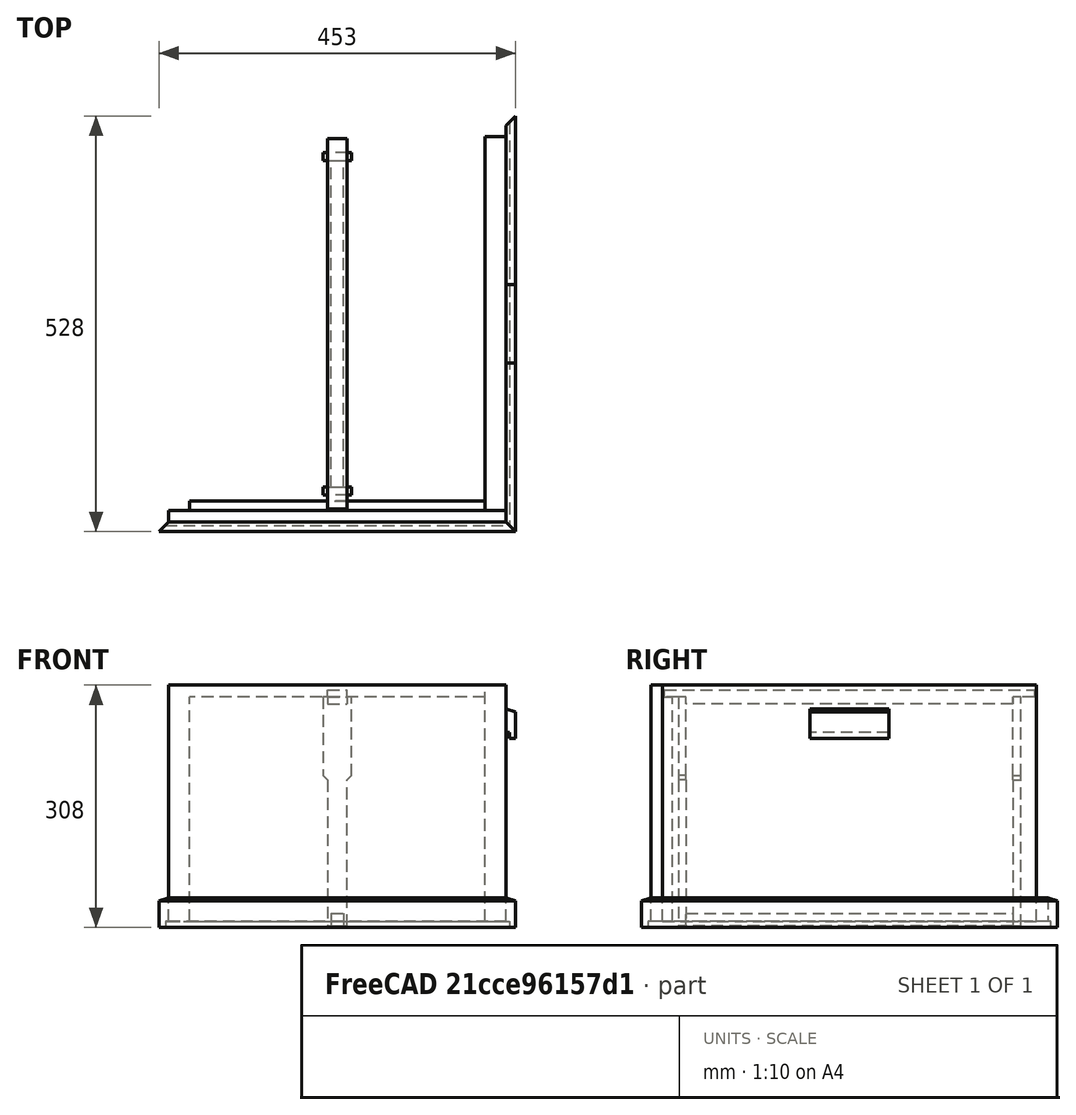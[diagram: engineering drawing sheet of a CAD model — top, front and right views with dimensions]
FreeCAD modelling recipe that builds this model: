
FCSTD DOCUMENT  (FreeCAD 0.19R)
Label: naklada
License: All rights reserved
LicenseURL: http://en.wikipedia.org/wiki/All_rights_reserved
objects: TechDraw::DrawViewDimension×33, App::Link×20, PartDesign::CoordinateSystem×16, Sketcher::SketchObject×12, TechDraw::DrawProjGroupItem×10, PartDesign::Pad×9, App::Part×7, PartDesign::Body×6, TechDraw::DrawProjGroup×5, TechDraw::DrawRichAnno×4, TechDraw::DrawViewPart×4, App::DocumentObjectGroup×3, PartDesign::Pocket×3, TechDraw::DrawSVGTemplate×3, TechDraw::DrawPage×3, TechDraw::DrawViewAnnotation×2, TechDraw::DrawViewSection×2, App::FeaturePython×1
note: 58 computed .brp shape members not serialized (recipe doc carries the construction recipe); baked Part::Feature solids carry a one-line shape summary decoded from their .brp

FEATURE [PartDesign::CoordinateSystem] LCS_Origin
  AttacherType = Attacher::AttachEngine3D
  MapMode = 2
  Support = -> [X_Axis]
FEATURE [App::FeaturePython] Variables  # WARN: FeaturePython — macro-defined, semantics opaque (R4)
  Type = App::PropertyContainer
  frame_cut = 15
  frame_height = 300
  frame_spacing = 37.5
  height = 300
  inner_depth = 450
  inner_width = 375
  wall_cut = 12.5
  wall_thickness = 27
FEATURE [App::DocumentObjectGroup] Constraints
FEATURE [App::DocumentObjectGroup] Configurations
FEATURE [PartDesign::CoordinateSystem] LCS_0
  AttacherType = Attacher::AttachEngine3D
  MapMode = 2
  Support = -> [X_Axis001]
FEATURE [PartDesign::CoordinateSystem] LCS_0001
  AttacherType = Attacher::AttachEngine3D
  MapMode = 2
  Support = -> [X_Axis002]
FEATURE [Sketcher::SketchObject] Sketch  label="Sketch001"
  FullyConstrained = true
  MapMode = 5
  Support = -> [XY_Plane002]
  expr: Constraints[16] = Variables.inner_width
  expr: Constraints[17] = Variables.wall_thickness
  expr: Constraints[22] = Variables.inner_depth / 2
  expr: Constraints[19] = Variables.wall_thickness
  expr: Constraints[18] = Variables.wall_cut
  sketch-geometry (8):
    g0: LineSegment StartX=-187.5 StartY=-225 StartZ=0 EndX=187.5 EndY=-225 EndZ=0
    g1: LineSegment StartX=187.5 StartY=-225 StartZ=0 EndX=187.5 EndY=-237.5 EndZ=0
    g2: LineSegment StartX=187.5 StartY=-237.5 StartZ=0 EndX=214.5 EndY=-237.5 EndZ=0
    g3: LineSegment StartX=214.5 StartY=-237.5 StartZ=0 EndX=214.5 EndY=-252 EndZ=0
    g4: LineSegment StartX=214.5 StartY=-252 StartZ=0 EndX=-214.5 EndY=-252 EndZ=0
    g5: LineSegment StartX=-214.5 StartY=-252 StartZ=0 EndX=-214.5 EndY=-237.5 EndZ=0
    g6: LineSegment StartX=-214.5 StartY=-237.5 StartZ=0 EndX=-187.5 EndY=-237.5 EndZ=0
    g7: LineSegment StartX=-187.5 StartY=-237.5 StartZ=0 EndX=-187.5 EndY=-225 EndZ=0
  constraints (23):
    c: Coincident(g0,g1)
    c: Coincident(g1,g2)
    c: Horizontal(g2)
    c: Coincident(g2,g3)
    c: Vertical(g3)
    c: Coincident(g3,g4)
    c: Horizontal(g4)
    c: Coincident(g4,g5)
    c: Vertical(g5)
    c: Coincident(g5,g6)
    c: Horizontal(g6)
    c: Coincident(g6,g7)
    c: Vertical(g7)
    c: Vertical(g1)
    c: Horizontal(g6,g1)
    c: Equal(g6,g2)
    c: DistanceX(g0,g0) = 375
    c: DistanceX(g2,g2) = 27
    c: DistanceY(g1,g1) = 12.5
    c: DistanceY(g3,g0) = 27
    c: Coincident(g0,g7)
    c: Symmetric(g0,g0,g-2)
    c: DistanceY(g0,g-1) = 225
FEATURE [PartDesign::Pad] Pad
  Direction = (1,1,1)
  Length = 300
  Length2 = 100
  Profile = -> Sketch
  Type = 0
  expr: Length = Variables.height
FEATURE [Sketcher::SketchObject] Sketch001  label="Sketch002"
  ExternalGeometry = -> [Pad]
  FullyConstrained = true
  MapMode = 5
  Placement = pos=(0,0,0) rot=(0.57735,0.57735,0.57735;2.0944rad)
  Support = -> [YZ_Plane002]
  expr: Constraints[9] = Variables.frame_cut
  sketch-geometry (4):
    g0: LineSegment StartX=-225 StartY=300 StartZ=0 EndX=-237.5 EndY=300 EndZ=0
    g1: LineSegment StartX=-237.5 StartY=300 StartZ=0 EndX=-237.5 EndY=285 EndZ=0
    g2: LineSegment StartX=-237.5 StartY=285 StartZ=0 EndX=-225 EndY=285 EndZ=0
    g3: LineSegment StartX=-225 StartY=285 StartZ=0 EndX=-225 EndY=300 EndZ=0
  constraints (10):
    c: Coincident(g0,g1)
    c: Coincident(g1,g2)
    c: Coincident(g2,g3)
    c: Coincident(g3,g0)
    c: Horizontal(g2)
    c: Vertical(g1)
    c: Vertical(g3)
    c: Coincident(g0,g-3)
    c: Coincident(g0,g-3)
    c: DistanceY(g3,g3) = 15
FEATURE [PartDesign::Pocket] Pocket
  BaseFeature = -> Pad
  Length = 5
  Length2 = 100
  Midplane = true
  Profile = -> Sketch001
  Type = 1
FEATURE [PartDesign::Body] Body
  Group = -> [LCS_0001,Sketch,Pad,Sketch001,Pocket]
  Origin = -> Origin002
  Tip = -> Pocket
FEATURE [App::Part] Wall_rear  label="wall_front_rear"
  Group = -> [LCS_0,Body]
  LabelDocUser = naklada
  LabelPartUser = Wall_rear
  Origin = -> Origin001
  PadLengthUser = 305.0 
  ShapeLengthUser = 890
  ShapeVolumeUser = 305.0 mm x 25.0 mm x 420.0 mm
FEATURE [App::Link] Wall_rear001  label="wall_front"
  AssemblyType = Part::Link
  AttachedBy = #LCS_0
  AttachedTo = Parent Assembly#LCS_Origin
  LinkedObject = -> Wall_rear
  SolverId = Asm4EE
  expr: Placement = LCS_Origin.Placement * AttachmentOffset * LCS_0.Placement ^ -1
FEATURE [App::Link] Wall_rear002  label="wall_rear"
  AssemblyType = Part::Link
  AttachedBy = #LCS_0
  AttachedTo = Parent Assembly#LCS_Origin
  AttachmentOffset = pos=(0,0,0) rot=(0,0,1;3.14159rad)
  LinkPlacement = pos=(0,0,0) rot=(0,0,1;3.14159rad)
  LinkedObject = -> Wall_rear
  Placement = pos=(0,0,0) rot=(0,0,1;3.14159rad)
  SolverId = Asm4EE
  expr: Placement = LCS_Origin.Placement * AttachmentOffset * LCS_0.Placement ^ -1
FEATURE [PartDesign::CoordinateSystem] LCS_0002  label="LCS_21"
  AttacherType = Attacher::AttachEngine3D
  MapMode = 2
  Support = -> [X_Axis003]
FEATURE [PartDesign::CoordinateSystem] LCS_0003
  AttacherType = Attacher::AttachEngine3D
  MapMode = 2
  Support = -> [X_Axis004]
FEATURE [Sketcher::SketchObject] Sketch002  label="Sketch003"
  FullyConstrained = true
  MapMode = 5
  Support = -> [XY_Plane004]
  expr: Constraints[6] = Variables.wall_thickness
  expr: Constraints[7] = Variables.inner_depth + Variables.wall_cut * 2
  expr: Constraints[8] = Variables.inner_width / 2
  sketch-geometry (4):
    g0: LineSegment StartX=187.5 StartY=-237.5 StartZ=0 EndX=214.5 EndY=-237.5 EndZ=0
    g1: LineSegment StartX=214.5 StartY=-237.5 StartZ=0 EndX=214.5 EndY=237.5 EndZ=0
    g2: LineSegment StartX=214.5 StartY=237.5 StartZ=0 EndX=187.5 EndY=237.5 EndZ=0
    g3: LineSegment StartX=187.5 StartY=237.5 StartZ=0 EndX=187.5 EndY=-237.5 EndZ=0
  constraints (11):
    c: Coincident(g0,g1)
    c: Coincident(g1,g2)
    c: Coincident(g2,g3)
    c: Coincident(g3,g0)
    c: Horizontal(g0)
    c: Horizontal(g2)
    c: DistanceX(g0,g0) = 27
    c: DistanceY(g1,g1) = 475
    c: DistanceX(g-1,g0) = 187.5
    c: Vertical(g1)
    c: Symmetric(g0,g2,g-1)
FEATURE [PartDesign::Pad] Pad001
  Direction = (1,1,1)
  Length = 300
  Length2 = 100
  Profile = -> Sketch002
  Type = 0
  expr: Length = Variables.height
FEATURE [PartDesign::Body] Body_2
  Group = -> [LCS_0003,Sketch002,Pad001]
  Origin = -> Origin004
  Tip = -> Pad001
FEATURE [App::Part] wall_side
  Group = -> [LCS_0002,Body_2]
  LabelDocUser = naklada
  LabelPartUser = wall_side
  Origin = -> Origin003
  PadLengthUser = 305.0 
  ShapeLengthUser = 1000
  ShapeVolumeUser = 305.0 mm x 475.0 mm x 25.0 mm
FEATURE [App::Link] wall_side001  label="wall_right"
  AssemblyType = Part::Link
  AttachedBy = #LCS_0002
  AttachedTo = Parent Assembly#LCS_Origin
  LinkedObject = -> wall_side
  SolverId = Asm4EE
  expr: Placement = LCS_Origin.Placement * AttachmentOffset * LCS_0002.Placement ^ -1
FEATURE [App::Link] wall  label="wall_left"
  AssemblyType = Part::Link
  AttachedBy = #LCS_0002
  AttachedTo = Parent Assembly#LCS_Origin
  AttachmentOffset = pos=(0,0,0) rot=(0,0,1;3.14159rad)
  LinkPlacement = pos=(0,0,0) rot=(0,0,1;3.14159rad)
  LinkedObject = -> wall_side
  Placement = pos=(0,0,0) rot=(0,0,1;3.14159rad)
  SolverId = Asm4EE
  expr: Placement = LCS_Origin.Placement * AttachmentOffset * LCS_0002.Placement ^ -1
FEATURE [PartDesign::CoordinateSystem] LCS_0004
  AttacherType = Attacher::AttachEngine3D
  MapMode = 2
  Support = -> [X_Axis005]
FEATURE [PartDesign::CoordinateSystem] LCS_0005
  AttacherType = Attacher::AttachEngine3D
  MapMode = 2
  Support = -> [X_Axis006]
FEATURE [Sketcher::SketchObject] Sketch003  label="Sketch004"
  FullyConstrained = true
  MapMode = 5
  Placement = pos=(0,0,0) rot=(1,0,0;1.5708rad)
  Support = -> [XZ_Plane006]
  expr: Constraints[12] = Variables.inner_width / 2 + Variables.wall_thickness
  sketch-geometry (6):
    g0: LineSegment StartX=214.5 StartY=0 StartZ=0 EndX=218.5 EndY=0 EndZ=0
    g1: LineSegment StartX=218.5 StartY=0 StartZ=0 EndX=218.5 EndY=-8 EndZ=0
    g2: LineSegment StartX=218.5 StartY=-8 StartZ=0 EndX=226.5 EndY=-8 EndZ=0
    g3: LineSegment StartX=226.5 StartY=-8 StartZ=0 EndX=226.5 EndY=25.6324 EndZ=0
    g4: LineSegment StartX=214.5 StartY=30 StartZ=0 EndX=214.5 EndY=0 EndZ=0
    g5: LineSegment StartX=214.5 StartY=30 StartZ=0 EndX=226.5 EndY=25.6324 EndZ=0
  constraints (18):
    c: Horizontal(g0)
    c: Coincident(g0,g1)
    c: Vertical(g1)
    c: Coincident(g1,g2)
    c: Horizontal(g2)
    c: Coincident(g2,g3)
    c: Vertical(g3)
    c: Coincident(g4,g0)
    c: Vertical(g4)
    c: DistanceX(g0,g0) = 4  'c'
    c: DistanceY(g1,g1) = 8  'd'
    c: Horizontal(g0,g-1)
    c: DistanceX(g-1,g0) = 214.5
    c: DistanceX(g0,g2) = 12  'a'
    c: DistanceY(g4,g4) = 30  'b'
    c: Coincident(g5,g4)
    c: Coincident(g5,g3)
    c: Angle(g5) = -0.349066  'e'
FEATURE [PartDesign::Pad] Pad002
  Direction = (1,1,1)
  Length = 700
  Length2 = 100
  Midplane = true
  Placement = pos=(0,0,0) rot=(1,0,0;1.5708rad)
  Profile = -> Sketch003
  Type = 0
FEATURE [Sketcher::SketchObject] Sketch004  label="Sketch005"
  ExternalGeometry = -> [Pad002]
  FullyConstrained = true
  MapMode = 5
  Support = -> [XY_Plane006]
  expr: Constraints[14] = Variables.inner_depth + 2 * Variables.wall_thickness
  sketch-geometry (8):
    g0: LineSegment StartX=226.5 StartY=-350 StartZ=0 EndX=226.5 EndY=-264 EndZ=0
    g1: LineSegment StartX=226.5 StartY=-264 StartZ=0 EndX=214.5 EndY=-252 EndZ=0
    g2: LineSegment StartX=214.5 StartY=-252 StartZ=0 EndX=214.5 EndY=-350 EndZ=0
    g3: LineSegment StartX=226.5 StartY=350 StartZ=0 EndX=226.5 EndY=264 EndZ=0
    g4: LineSegment StartX=226.5 StartY=264 StartZ=0 EndX=214.5 EndY=252 EndZ=0
    g5: LineSegment StartX=214.5 StartY=252 StartZ=0 EndX=214.5 EndY=350 EndZ=0
    g6: LineSegment StartX=214.5 StartY=-350 StartZ=0 EndX=226.5 EndY=-350 EndZ=0
    g7: LineSegment StartX=214.5 StartY=350 StartZ=0 EndX=226.5 EndY=350 EndZ=0
  constraints (20):
    c: Coincident(g0,g-4)
    c: Coincident(g1,g0)
    c: Coincident(g2,g1)
    c: Coincident(g2,g-4)
    c: Vertical(g2)
    c: Vertical(g0)
    c: Coincident(g-3,g3)
    c: Vertical(g3)
    c: Coincident(g3,g4)
    c: Coincident(g4,g5)
    c: Coincident(g5,g-3)
    c: Vertical(g5)
    c: Equal(g4,g1)
    c: Equal(g5,g2)
    c: DistanceY(g1,g4) = 504
    c: Coincident(g6,g2)
    c: Coincident(g6,g0)
    c: Coincident(g7,g5)
    c: Coincident(g7,g3)
    c: Perpendicular(g4,g1)
FEATURE [PartDesign::Pocket] Pocket001
  BaseFeature = -> Pad002
  Length = 41
  Length2 = 100
  Midplane = true
  Placement = pos=(0,0,0) rot=(1,0,0;1.5708rad)
  Profile = -> Sketch004
  Type = 1
FEATURE [PartDesign::Body] Body_3
  Group = -> [LCS_0005,Sketch003,Pad002,Sketch004,Pocket001]
  Origin = -> Origin006
  Tip = -> Pocket001
FEATURE [App::Part] Slat  label="slat_side"
  Group = -> [LCS_0004,Body_3]
  Origin = -> Origin005
FEATURE [PartDesign::CoordinateSystem] LCS_0006
  AttacherType = Attacher::AttachEngine3D
  MapMode = 2
  Support = -> [X_Axis007]
FEATURE [PartDesign::CoordinateSystem] LCS_0007
  AttacherType = Attacher::AttachEngine3D
  MapMode = 2
  Support = -> [X_Axis008]
FEATURE [Sketcher::SketchObject] Sketch005  label="Sketch006"
  FullyConstrained = true
  MapMode = 5
  Placement = pos=(0,0,0) rot=(0.57735,0.57735,0.57735;2.0944rad)
  Support = -> [YZ_Plane008]
  expr: Constraints[17] = Variables.inner_depth / 2 + Variables.wall_thickness
  sketch-geometry (6):
    g0: LineSegment StartX=-252 StartY=0 StartZ=0 EndX=-252 EndY=30 EndZ=0
    g1: LineSegment StartX=-264 StartY=25.6324 StartZ=0 EndX=-264 EndY=-8 EndZ=0
    g2: LineSegment StartX=-264 StartY=-8 StartZ=0 EndX=-256 EndY=-8 EndZ=0
    g3: LineSegment StartX=-256 StartY=-8 StartZ=0 EndX=-256 EndY=0 EndZ=0
    g4: LineSegment StartX=-256 StartY=0 StartZ=0 EndX=-252 EndY=0 EndZ=0
    g5: LineSegment StartX=-264 StartY=25.6324 StartZ=0 EndX=-252 EndY=30 EndZ=0
  constraints (18):
    c: Vertical(g0)
    c: Vertical(g1)
    c: Coincident(g1,g2)
    c: Horizontal(g2)
    c: Coincident(g2,g3)
    c: Vertical(g3)
    c: Coincident(g3,g4)
    c: Coincident(g4,g0)
    c: Horizontal(g4)
    c: Horizontal(g0,g-1)
    c: DistanceX(g4,g4) = 4
    c: DistanceY(g3,g3) = 8
    c: DistanceX(g1,g0) = 12
    c: DistanceY(g0,g0) = 30
    c: Coincident(g5,g1)
    c: Coincident(g5,g0)
    c: Angle(g5) = 0.349066
    c: DistanceX(g0,g-1) = 252
FEATURE [PartDesign::Pad] Pad003
  Direction = (1,1,1)
  Length = 700
  Length2 = 100
  Midplane = true
  Placement = pos=(0,0,0) rot=(0.57735,0.57735,0.57735;2.0944rad)
  Profile = -> Sketch005
  Type = 0
FEATURE [Sketcher::SketchObject] Sketch006  label="Sketch007"
  ExternalGeometry = -> [Pad003]
  FullyConstrained = true
  MapMode = 5
  Support = -> [XY_Plane008]
  expr: Constraints[19] = Variables.inner_width + 2 * Variables.wall_thickness
  sketch-geometry (8):
    g0: LineSegment StartX=-350 StartY=-264 StartZ=0 EndX=-350 EndY=-252 EndZ=0
    g1: LineSegment StartX=-350 StartY=-252 StartZ=0 EndX=-214.5 EndY=-252 EndZ=0
    g2: LineSegment StartX=-214.5 StartY=-252 StartZ=0 EndX=-226.5 EndY=-264 EndZ=0
    g3: LineSegment StartX=-226.5 StartY=-264 StartZ=0 EndX=-350 EndY=-264 EndZ=0
    g4: LineSegment StartX=350 StartY=-264 StartZ=0 EndX=350 EndY=-252 EndZ=0
    g5: LineSegment StartX=350 StartY=-252 StartZ=0 EndX=214.5 EndY=-252 EndZ=0
    g6: LineSegment StartX=214.5 StartY=-252 StartZ=0 EndX=226.5 EndY=-264 EndZ=0
    g7: LineSegment StartX=226.5 StartY=-264 StartZ=0 EndX=350 EndY=-264 EndZ=0
  constraints (20):
    c: Coincident(g-3,g0)
    c: Coincident(g0,g-3)
    c: Coincident(g0,g1)
    c: Coincident(g1,g2)
    c: Coincident(g2,g3)
    c: Coincident(g3,g0)
    c: Coincident(g-4,g4)
    c: Coincident(g4,g-4)
    c: Coincident(g4,g5)
    c: Coincident(g5,g6)
    c: Coincident(g6,g7)
    c: Coincident(g7,g4)
    c: Perpendicular(g2,g6)
    c: Equal(g2,g6)
    c: Equal(g1,g5)
    c: Horizontal(g1)
    c: Horizontal(g3)
    c: Horizontal(g7)
    c: Horizontal(g5)
    c: DistanceX(g1,g5) = 429
FEATURE [PartDesign::Pocket] Pocket002
  BaseFeature = -> Pad003
  Length = 5
  Length2 = 100
  Midplane = true
  Placement = pos=(0,0,0) rot=(0.57735,0.57735,0.57735;2.0944rad)
  Profile = -> Sketch006
  Type = 1
FEATURE [PartDesign::Body] Body_4
  Group = -> [LCS_0007,Sketch005,Pad003,Sketch006,Pocket002]
  Origin = -> Origin008
  Tip = -> Pocket002
FEATURE [App::Part] Slat2  label="slat_front_rear"
  Group = -> [LCS_0006,Body_4]
  Origin = -> Origin007
FEATURE [App::Link] Slat003  label="slat_right"
  AssemblyType = Part::Link
  AttachedBy = #LCS_0004
  AttachedTo = Parent Assembly#LCS_Origin
  LinkedObject = -> Slat
  SolverId = Asm4EE
  expr: Placement = LCS_Origin.Placement * AttachmentOffset * LCS_0004.Placement ^ -1
FEATURE [App::Link] Slat2001  label="slat_front"
  AssemblyType = Part::Link
  AttachedBy = #LCS_0006
  AttachedTo = Parent Assembly#LCS_Origin
  LinkedObject = -> Slat2
  SolverId = Asm4EE
  expr: Placement = LCS_Origin.Placement * AttachmentOffset * LCS_0006.Placement ^ -1
FEATURE [App::Link] Slat2002  label="slat_left"
  AssemblyType = Part::Link
  AttachedBy = #LCS_0004
  AttachedTo = Parent Assembly#LCS_Origin
  AttachmentOffset = pos=(0,0,0) rot=(0,0,1;3.14159rad)
  LinkPlacement = pos=(0,0,0) rot=(0,0,1;3.14159rad)
  LinkedObject = -> Slat
  Placement = pos=(0,0,0) rot=(0,0,1;3.14159rad)
  SolverId = Asm4EE
  expr: Placement = LCS_Origin.Placement * AttachmentOffset * LCS_0004.Placement ^ -1
FEATURE [App::Link] Slat2003  label="slat_rear"
  AssemblyType = Part::Link
  AttachedBy = #LCS_0006
  AttachedTo = Parent Assembly#LCS_Origin
  AttachmentOffset = pos=(0,0,0) rot=(0,0,1;3.14159rad)
  LinkPlacement = pos=(0,0,0) rot=(0,0,1;3.14159rad)
  LinkedObject = -> Slat2
  Placement = pos=(0,0,0) rot=(0,0,1;3.14159rad)
  SolverId = Asm4EE
  expr: Placement = LCS_Origin.Placement * AttachmentOffset * LCS_0006.Placement ^ -1
FEATURE [TechDraw::DrawSVGTemplate] Template
  EditableTexts = AVTOR=Brane Borštnik; AVTOR_2=Risal: Janez Paternoster; DATUM=6.5.2022; MATERIAL=Les, smreka; MERILO=1:5; NAZIV=Naklada; NAZIV_2=Dadant-Blatt panj; STRAN=Stran 1/3; VIR=https://github.com/<owner>/Dadant-Blatt
  Height = 297
  Orientation = 0
  Width = 210
FEATURE [Sketcher::SketchObject] Sketch007  label="Sketch008"
  FullyConstrained = true
  MapMode = 5
  Placement = pos=(0,0,0) rot=(1,0,0;1.5708rad)
  Support = -> [XZ_Plane009]
  expr: Constraints[11] = Variables.inner_width / 2 + Variables.wall_thickness
  expr: Constraints[17] = Variables.height - 30
  sketch-geometry (6):
    g0: LineSegment StartX=214.5 StartY=240 StartZ=0 EndX=218.5 EndY=240 EndZ=0
    g1: LineSegment StartX=218.5 StartY=240 StartZ=0 EndX=218.5 EndY=232 EndZ=0
    g2: LineSegment StartX=218.5 StartY=232 StartZ=0 EndX=226.5 EndY=232 EndZ=0
    g3: LineSegment StartX=226.5 StartY=232 StartZ=0 EndX=226.5 EndY=265.632 EndZ=0
    g4: LineSegment StartX=214.5 StartY=270 StartZ=0 EndX=214.5 EndY=240 EndZ=0
    g5: LineSegment StartX=214.5 StartY=270 StartZ=0 EndX=226.5 EndY=265.632 EndZ=0
  constraints (18):
    c: Horizontal(g0)
    c: Coincident(g0,g1)
    c: Vertical(g1)
    c: Coincident(g1,g2)
    c: Horizontal(g2)
    c: Coincident(g2,g3)
    c: Vertical(g3)
    c: Coincident(g4,g0)
    c: Vertical(g4)
    c: DistanceX(g0,g0) = 4  'c'
    c: DistanceY(g1,g1) = 8  'd'
    c: DistanceX(g-1,g0) = 214.5
    c: DistanceX(g0,g2) = 12  'a'
    c: DistanceY(g4,g4) = 30  'b'
    c: Coincident(g5,g4)
    c: Coincident(g5,g3)
    c: Angle(g5) = -0.349066  'e'
    c: DistanceY(g-1,g4) = 270
FEATURE [PartDesign::CoordinateSystem] LCS_0008
  AttacherType = Attacher::AttachEngine3D
  MapMode = 2
  Support = -> [X_Axis010]
FEATURE [PartDesign::CoordinateSystem] LCS_0009
  AttacherType = Attacher::AttachEngine3D
  MapMode = 2
  Support = -> [X_Axis009]
FEATURE [PartDesign::Pad] Pad004
  Direction = (1,1,1)
  Length = 100
  Length2 = 100
  Midplane = true
  Placement = pos=(0,0,0) rot=(1,0,0;1.5708rad)
  Profile = -> Sketch007
  Type = 0
FEATURE [PartDesign::Body] Body_005
  Group = -> [LCS_0008,Sketch007,Pad004]
  Origin = -> Origin009
  Tip = -> Pad004
FEATURE [App::Part] Slat2004  label="handle"
  Group = -> [LCS_0009,Body_005]
  Origin = -> Origin010
FEATURE [App::Link] Handle1  label="handle_right"
  AssemblyType = Part::Link
  AttachedBy = #LCS_0009
  AttachedTo = Parent Assembly#LCS_Origin
  LinkedObject = -> Slat2004
  SolverId = Asm4EE
  expr: Placement = LCS_Origin.Placement * AttachmentOffset * LCS_0009.Placement ^ -1
FEATURE [App::Link] Handle2  label="handle_left"
  AssemblyType = Part::Link
  AttachedBy = #LCS_0009
  AttachedTo = Parent Assembly#LCS_Origin
  AttachmentOffset = pos=(0,0,0) rot=(0,0,1;3.14159rad)
  LinkPlacement = pos=(0,0,0) rot=(0,0,1;3.14159rad)
  LinkedObject = -> Slat2004
  Placement = pos=(0,0,0) rot=(0,0,1;3.14159rad)
  SolverId = Asm4EE
  expr: Placement = LCS_Origin.Placement * AttachmentOffset * LCS_0009.Placement ^ -1
FEATURE [TechDraw::DrawSVGTemplate] Template001
  EditableTexts = AVTOR=Brane Borštnik; AVTOR_2=Risal: Janez Paternoster; DATUM=6.5.2022; MATERIAL=Les, smreka; MERILO=1:5; NAZIV=Naklada; NAZIV_2=Dadant-Blatt panj; STRAN=Stran 2/3; VIR=https://github.com/<owner>/Dadant-Blatt
  Height = 297
  Orientation = 0
  Width = 210
FEATURE [TechDraw::DrawProjGroupItem] ProjItem  label="Front"
  CoarseView = false
  Direction = (0,1,0)
  Focus = 100
  HardHidden = false
  IsoCount = 0
  IsoHidden = false
  IsoVisible = false
  LockPosition = true
  Perspective = false
  Rotation = 0
  RotationVector = (-1,0,0)
  Scale = 0.2
  ScaleType = 2
  SeamHidden = false
  SeamVisible = true
  SmoothHidden = false
  SmoothVisible = true
  Source = -> [Wall_rear]
  Type = 0
  X = 0
  XDirection = (-1,0,0)
  Y = 0
FEATURE [TechDraw::DrawProjGroupItem] ProjItem001  label="Left"
  CoarseView = false
  Direction = (1,1e-16,0)
  Focus = 100
  HardHidden = false
  IsoCount = 0
  IsoHidden = false
  IsoVisible = false
  LockPosition = false
  Perspective = false
  Rotation = 0
  RotationVector = (1,0,0)
  Scale = 0.2
  ScaleType = 2
  SeamHidden = false
  SeamVisible = true
  SmoothHidden = false
  SmoothVisible = true
  Source = -> [Wall_rear]
  Type = 1
  X = 75.6
  XDirection = (-1e-16,1,0)
  Y = 0
FEATURE [TechDraw::DrawProjGroup] ProjGroup
  Anchor = -> ProjItem
  AutoDistribute = true
  LockPosition = false
  ProjectionType = 0
  Rotation = 0
  Scale = 0.2
  ScaleType = 0
  Source = -> [Wall_rear]
  Views = -> [ProjItem,ProjItem001]
  X = 94.3849
  Y = 230.952
  spacingX = 30
  spacingY = 15
FEATURE [TechDraw::DrawViewDimension] Dimension009
  Arbitrary = false
  ArbitraryTolerances = false
  EqualTolerance = true
  FormatSpec = %.6g
  FormatSpecOverTolerance = %+.6g
  FormatSpecUnderTolerance = %+.6g
  Inverted = false
  LockPosition = false
  MeasureType = 1
  OverTolerance = 0
  References2D = -> [ProjItem]
  Rotation = 0
  ScaleType = 0
  TheoreticalExact = false
  Type = 1
  UnderTolerance = 0
  X = -0.502911
  Y = 52.7957
FEATURE [TechDraw::DrawViewDimension] Dimension010
  Arbitrary = false
  ArbitraryTolerances = false
  EqualTolerance = true
  FormatSpec = %.6g
  FormatSpecOverTolerance = %+.6g
  FormatSpecUnderTolerance = %+.6g
  Inverted = false
  LockPosition = false
  MeasureType = 1
  OverTolerance = 0
  References2D = -> [ProjItem]
  Rotation = 0
  ScaleType = 0
  TheoreticalExact = false
  Type = 1
  UnderTolerance = 0
  X = -0.502911
  Y = 44.9343
FEATURE [TechDraw::DrawViewDimension] Dimension011
  Arbitrary = false
  ArbitraryTolerances = false
  EqualTolerance = true
  FormatSpec = H = %.6g ali 200 ali 175
  FormatSpecOverTolerance = %+.6g
  FormatSpecUnderTolerance = %+.6g
  Inverted = false
  LockPosition = false
  MeasureType = 1
  OverTolerance = 0
  References2D = -> [ProjItem]
  Rotation = 0
  ScaleType = 0
  TheoreticalExact = false
  Type = 2
  UnderTolerance = 0
  X = -64.9634
  Y = 0
FEATURE [TechDraw::DrawViewDimension] Dimension013
  Arbitrary = false
  ArbitraryTolerances = false
  EqualTolerance = true
  FormatSpec = (%.6g)
  FormatSpecOverTolerance = %+.6g
  FormatSpecUnderTolerance = %+.6g
  Inverted = false
  LockPosition = false
  MeasureType = 1
  OverTolerance = 0
  References2D = -> [ProjItem]
  Rotation = 0
  ScaleType = 0
  TheoreticalExact = false
  Type = 1
  UnderTolerance = 0
  X = 51.7346
  Y = 44.9168
FEATURE [TechDraw::DrawViewDimension] Dimension014
  Arbitrary = false
  ArbitraryTolerances = false
  EqualTolerance = true
  FormatSpec = %.6g
  FormatSpecOverTolerance = %+.6g
  FormatSpecUnderTolerance = %+.6g
  Inverted = false
  LockPosition = false
  MeasureType = 1
  OverTolerance = 0
  References2D = -> [ProjItem001]
  Rotation = 0
  ScaleType = 0
  TheoreticalExact = false
  Type = 1
  UnderTolerance = 0
  X = 10.47
  Y = 52.6456
FEATURE [TechDraw::DrawViewDimension] Dimension015
  Arbitrary = false
  ArbitraryTolerances = false
  EqualTolerance = true
  FormatSpec = %.6g
  FormatSpecOverTolerance = %+.6g
  FormatSpecUnderTolerance = %+.6g
  Inverted = false
  LockPosition = false
  MeasureType = 1
  OverTolerance = 0
  References2D = -> [ProjItem001]
  Rotation = 0
  ScaleType = 0
  TheoreticalExact = false
  Type = 1
  UnderTolerance = 0
  X = 11.2317
  Y = 44.9255
FEATURE [TechDraw::DrawRichAnno] RichTextAnnotation
  AnnoParent = -> ProjItem
  AnnoText = <!DOCTYPE HTML PUBLIC "-//W3C//DTD HTML 4.0//EN" "http://www.w3.org/TR/REC-html40/strict.dtd">\n<html><head><meta name="qrichtext" content="1" /><style type="text/css">\np, li { white-space: pre-wrap; }\n</style></head><body style=" font-family:'Ubuntu'; font-size:11pt; font-weight:400; font-style:normal;">\n<p style=" margin-top:0px; margin-bottom:0px; margin-left:0px; margin-right:0px; -qt-block-indent:0; text-indent:0px;"><span style=" font-size:10pt;">Sprednja in</span></p>\n<p style=" margin-top:0px; margin-bottom:0px; margin-left:0px; margin-right:0px; -qt-block-indent:0; text-indent:0px;"><span style=" font-size:10pt;">zadnja stranica</span></p></body></html>
  LockPosition = false
  MaxWidth = -1
  Rotation = 0
  ScaleType = 0
  ShowFrame = false
  X = 0
  Y = 0
FEATURE [TechDraw::DrawProjGroupItem] ProjItem002  label="Front001"
  CoarseView = false
  Direction = (1,0,0)
  Focus = 100
  HardHidden = false
  IsoCount = 0
  IsoHidden = false
  IsoVisible = false
  LockPosition = true
  Perspective = false
  Rotation = 0
  RotationVector = (0,1,0)
  Scale = 0.2
  ScaleType = 2
  SeamHidden = false
  SeamVisible = true
  SmoothHidden = false
  SmoothVisible = true
  Source = -> [wall_side]
  Type = 0
  X = 0
  XDirection = (0,1,0)
  Y = 0
FEATURE [TechDraw::DrawProjGroupItem] ProjItem003  label="Left001"
  CoarseView = false
  Direction = (1e-16,-1,0)
  Focus = 100
  HardHidden = false
  IsoCount = 0
  IsoHidden = false
  IsoVisible = false
  LockPosition = false
  Perspective = false
  Rotation = 0
  RotationVector = (1,0,0)
  Scale = 0.2
  ScaleType = 2
  SeamHidden = false
  SeamVisible = true
  SmoothHidden = false
  SmoothVisible = true
  Source = -> [wall_side]
  Type = 1
  X = 80.2
  XDirection = (1,1e-16,0)
  Y = 0
FEATURE [TechDraw::DrawProjGroup] ProjGroup001
  Anchor = -> ProjItem002
  AutoDistribute = true
  LockPosition = false
  ProjectionType = 0
  Rotation = 0
  Scale = 0.2
  ScaleType = 0
  Source = -> [wall_side]
  Views = -> [ProjItem002,ProjItem003]
  X = 91.8443
  Y = 140.877
  spacingX = 30
  spacingY = 15
FEATURE [TechDraw::DrawViewDimension] Dimension016
  Arbitrary = false
  ArbitraryTolerances = false
  EqualTolerance = true
  FormatSpec = %.6g
  FormatSpecOverTolerance = %+.6g
  FormatSpecUnderTolerance = %+.6g
  Inverted = false
  LockPosition = false
  MeasureType = 1
  OverTolerance = 0
  References2D = -> [ProjItem002]
  Rotation = 0
  ScaleType = 0
  TheoreticalExact = false
  Type = 1
  UnderTolerance = 0
  X = -0.317325
  Y = 40.9717
FEATURE [TechDraw::DrawViewDimension] Dimension017
  Arbitrary = false
  ArbitraryTolerances = false
  EqualTolerance = true
  FormatSpec = H = %.6g ali 200 ali 175
  FormatSpecOverTolerance = %+.6g
  FormatSpecUnderTolerance = %+.6g
  Inverted = false
  LockPosition = false
  MeasureType = 1
  OverTolerance = 0
  References2D = -> [ProjItem002]
  Rotation = 0
  ScaleType = 0
  TheoreticalExact = false
  Type = 2
  UnderTolerance = 0
  X = -57.9717
  Y = -0.317325
FEATURE [TechDraw::DrawViewDimension] Dimension018
  Arbitrary = false
  ArbitraryTolerances = false
  EqualTolerance = true
  FormatSpec = %.6g
  FormatSpecOverTolerance = %+.6g
  FormatSpecUnderTolerance = %+.6g
  Inverted = false
  LockPosition = false
  MeasureType = 1
  OverTolerance = 0
  References2D = -> [ProjItem003]
  Rotation = 0
  ScaleType = 0
  TheoreticalExact = false
  Type = 1
  UnderTolerance = 0
  X = -0.317325
  Y = 42.5584
FEATURE [TechDraw::DrawRichAnno] RichTextAnnotation001
  AnnoParent = -> ProjItem002
  AnnoText = <!DOCTYPE HTML PUBLIC "-//W3C//DTD HTML 4.0//EN" "http://www.w3.org/TR/REC-html40/strict.dtd">\n<html><head><meta name="qrichtext" content="1" /><style type="text/css">\np, li { white-space: pre-wrap; }\n</style></head><body style=" font-family:'Ubuntu'; font-size:11pt; font-weight:400; font-style:normal;">\n<p style=" margin-top:0px; margin-bottom:0px; margin-left:0px; margin-right:0px; -qt-block-indent:0; text-indent:0px;"><span style=" font-size:10pt;">Leva in desna</span></p>\n<p style=" margin-top:0px; margin-bottom:0px; margin-left:0px; margin-right:0px; -qt-block-indent:0; text-indent:0px;"><span style=" font-size:10pt;">stranica</span></p></body></html>
  LockPosition = false
  MaxWidth = -1
  Rotation = 0
  ScaleType = 0
  ShowFrame = false
  X = 0
  Y = 0
FEATURE [TechDraw::DrawProjGroupItem] ProjItem004  label="Front002"
  CoarseView = false
  Direction = (0,0,1)
  Focus = 100
  HardHidden = false
  IsoCount = 0
  IsoHidden = false
  IsoVisible = false
  LockPosition = true
  Perspective = false
  Rotation = 0
  RotationVector = (1,0,0)
  Scale = 0.2
  ScaleType = 2
  SeamHidden = false
  SeamVisible = true
  SmoothHidden = false
  SmoothVisible = true
  Source = -> [Slat]
  Type = 0
  X = 0
  XDirection = (1e-16,1,0)
  Y = 0
FEATURE [TechDraw::DrawProjGroupItem] ProjItem005  label="Left002"
  CoarseView = false
  Direction = (-1e-16,-1,1e-16)
  Focus = 100
  HardHidden = false
  IsoCount = 0
  IsoHidden = false
  IsoVisible = false
  LockPosition = false
  Perspective = false
  Rotation = 0
  RotationVector = (1,0,0)
  Scale = 0.2
  ScaleType = 2
  SeamHidden = false
  SeamVisible = true
  SmoothHidden = false
  SmoothVisible = true
  Source = -> [Slat]
  Type = 1
  X = 66.6
  XDirection = (0,1e-16,1)
  Y = 0
FEATURE [TechDraw::DrawProjGroup] ProjGroup002
  Anchor = -> ProjItem004
  AutoDistribute = true
  LockPosition = false
  ProjectionType = 0
  Rotation = 0
  Scale = 0.2
  ScaleType = 0
  Source = -> [Slat]
  Views = -> [ProjItem004,ProjItem005]
  X = 75.6556
  Y = 77.8761
  spacingX = 10
  spacingY = 15
FEATURE [TechDraw::DrawProjGroupItem] ProjItem006  label="Front003"
  CoarseView = false
  Direction = (0,0,1)
  Focus = 100
  HardHidden = false
  IsoCount = 0
  IsoHidden = false
  IsoVisible = false
  LockPosition = true
  Perspective = false
  Rotation = 0
  RotationVector = (1,0,0)
  Scale = 0.2
  ScaleType = 2
  SeamHidden = false
  SeamVisible = true
  SmoothHidden = false
  SmoothVisible = true
  Source = -> [Slat2]
  Type = 0
  X = 0
  XDirection = (1,0,0)
  Y = 0
FEATURE [TechDraw::DrawProjGroupItem] ProjItem007  label="Left003"
  CoarseView = false
  Direction = (-1,0,1e-16)
  Focus = 100
  HardHidden = false
  IsoCount = 0
  IsoHidden = false
  IsoVisible = false
  LockPosition = false
  Perspective = false
  Rotation = 0
  RotationVector = (1,0,0)
  Scale = 0.2
  ScaleType = 2
  SeamHidden = false
  SeamVisible = true
  SmoothHidden = false
  SmoothVisible = true
  Source = -> [Slat2]
  Type = 1
  X = 59.1
  XDirection = (1e-16,0,1)
  Y = 0
FEATURE [TechDraw::DrawProjGroup] ProjGroup003
  Anchor = -> ProjItem006
  AutoDistribute = true
  LockPosition = false
  ProjectionType = 0
  Rotation = 0
  Scale = 0.2
  ScaleType = 0
  Source = -> [Slat2]
  Views = -> [ProjItem006,ProjItem007]
  X = 68.8614
  Y = 60.7437
  spacingX = 10
  spacingY = 15
FEATURE [TechDraw::DrawProjGroupItem] ProjItem008  label="Front004"
  CoarseView = false
  Direction = (0,0,1)
  Focus = 100
  HardHidden = false
  IsoCount = 0
  IsoHidden = false
  IsoVisible = false
  LockPosition = true
  Perspective = false
  Rotation = 0
  RotationVector = (1,0,0)
  Scale = 0.2
  ScaleType = 2
  SeamHidden = false
  SeamVisible = true
  SmoothHidden = false
  SmoothVisible = true
  Source = -> [Slat2004]
  Type = 0
  X = 0
  XDirection = (1e-16,1,0)
  Y = 0
FEATURE [TechDraw::DrawProjGroupItem] ProjItem009  label="Left004"
  CoarseView = false
  Direction = (-1e-16,-1,1e-16)
  Focus = 100
  HardHidden = false
  IsoCount = 0
  IsoHidden = false
  IsoVisible = false
  LockPosition = false
  Perspective = false
  Rotation = 0
  RotationVector = (1,0,0)
  Scale = 0.2
  ScaleType = 2
  SeamHidden = false
  SeamVisible = true
  SmoothHidden = false
  SmoothVisible = true
  Source = -> [Slat2004]
  Type = 1
  X = 23.8
  XDirection = (0,1e-16,1)
  Y = 0
FEATURE [TechDraw::DrawProjGroup] ProjGroup004
  Anchor = -> ProjItem008
  AutoDistribute = true
  LockPosition = false
  ProjectionType = 0
  Rotation = 0
  Scale = 0.2
  ScaleType = 0
  Source = -> [Slat2004]
  Views = -> [ProjItem008,ProjItem009]
  X = 35.3841
  Y = 39.8465
  spacingX = 10
  spacingY = 15
FEATURE [TechDraw::DrawViewDimension] Dimension021
  Arbitrary = false
  ArbitraryTolerances = false
  EqualTolerance = true
  FormatSpec = %.6g
  FormatSpecOverTolerance = %+.6g
  FormatSpecUnderTolerance = %+.6g
  Inverted = false
  LockPosition = false
  MeasureType = 1
  OverTolerance = 0
  References2D = -> [ProjItem008]
  Rotation = 0
  ScaleType = 0
  TheoreticalExact = false
  Type = 1
  UnderTolerance = 0
  X = 0.661094
  Y = 12.0219
FEATURE [TechDraw::DrawViewPart] View002
  CoarseView = false
  Direction = (0,-1,0)
  Focus = 100
  HardHidden = false
  IsoCount = 0
  IsoHidden = false
  IsoVisible = false
  LockPosition = false
  Perspective = false
  Rotation = 0
  ScaleType = 0
  SeamHidden = false
  SeamVisible = true
  SmoothHidden = false
  SmoothVisible = true
  Source = -> [Slat2004]
  X = 181.026
  XDirection = (1,0,0)
  Y = 58.2571
FEATURE [TechDraw::DrawViewAnnotation] Annotation
  Font = osifont
  LineSpace = 80
  LockPosition = false
  MaxWidth = -1
  Rotation = 0
  ScaleType = 0
  Text = Spodnje letvice in ro\u010daji, po 2x:
  TextSize = 5
  TextStyle = 0
  X = 57.781
  Y = 93.0138
FEATURE [TechDraw::DrawViewDimension] Dimension022
  Arbitrary = false
  ArbitraryTolerances = false
  EqualTolerance = true
  FormatSpec = %.6g
  FormatSpecOverTolerance = %+.6g
  FormatSpecUnderTolerance = %+.6g
  Inverted = false
  LockPosition = false
  MeasureType = 1
  OverTolerance = 0
  References2D = -> [View002]
  Rotation = 0
  ScaleType = 0
  TheoreticalExact = false
  Type = 1
  UnderTolerance = 0
  X = -0.235593
  Y = 33.2252
FEATURE [TechDraw::DrawViewDimension] Dimension023
  Arbitrary = false
  ArbitraryTolerances = false
  EqualTolerance = true
  FormatSpec = %.6g
  FormatSpecOverTolerance = %+.6g
  FormatSpecUnderTolerance = %+.6g
  Inverted = false
  LockPosition = false
  MeasureType = 1
  OverTolerance = 0
  References2D = -> [ProjItem004]
  Rotation = 0
  ScaleType = 0
  TheoreticalExact = false
  Type = 1
  UnderTolerance = 0
  X = -0.440729
  Y = 11.1164
FEATURE [TechDraw::DrawViewDimension] Dimension024
  Arbitrary = false
  ArbitraryTolerances = false
  EqualTolerance = true
  FormatSpec = %.6g
  FormatSpecOverTolerance = %+.6g
  FormatSpecUnderTolerance = %+.6g
  Inverted = false
  LockPosition = false
  MeasureType = 1
  OverTolerance = 0
  References2D = -> [ProjItem006]
  Rotation = 0
  ScaleType = 0
  TheoreticalExact = false
  Type = 1
  UnderTolerance = 0
  X = 0
  Y = 12.659
FEATURE [TechDraw::DrawRichAnno] RichTextAnnotation002
  AnnoParent = -> View002
  AnnoText = <!DOCTYPE HTML PUBLIC "-//W3C//DTD HTML 4.0//EN" "http://www.w3.org/TR/REC-html40/strict.dtd">\n<html><head><meta name="qrichtext" content="1" /><style type="text/css">\np, li { white-space: pre-wrap; }\n</style></head><body style=" font-family:'Ubuntu'; font-size:11pt; font-weight:400; font-style:normal;">\n<p style=" margin-top:0px; margin-bottom:0px; margin-left:0px; margin-right:0px; -qt-block-indent:0; text-indent:0px;"><span style=" font-size:10pt;">M 1:1</span></p></body></html>
  LockPosition = false
  MaxWidth = -1
  Rotation = 0
  ScaleType = 0
  ShowFrame = false
  X = 0
  Y = 0
FEATURE [TechDraw::DrawViewDimension] Dimension025
  Arbitrary = false
  ArbitraryTolerances = false
  EqualTolerance = true
  FormatSpec = %.6g
  FormatSpecOverTolerance = %+.6g
  FormatSpecUnderTolerance = %+.6g
  Inverted = false
  LockPosition = false
  MeasureType = 1
  OverTolerance = 0
  References2D = -> [View002]
  Rotation = 0
  ScaleType = 0
  TheoreticalExact = false
  Type = 2
  UnderTolerance = 0
  X = -22.9514
  Y = 0.220364
FEATURE [TechDraw::DrawViewDimension] Dimension026
  Arbitrary = false
  ArbitraryTolerances = false
  EqualTolerance = true
  FormatSpec = %.6g
  FormatSpecOverTolerance = %+.6g
  FormatSpecUnderTolerance = %+.6g
  Inverted = false
  LockPosition = false
  MeasureType = 1
  OverTolerance = 0
  References2D = -> [View002]
  Rotation = 0
  ScaleType = 0
  TheoreticalExact = false
  Type = 2
  UnderTolerance = 0
  X = -14.3404
  Y = -12.7964
FEATURE [TechDraw::DrawViewDimension] Dimension027
  Arbitrary = false
  ArbitraryTolerances = false
  EqualTolerance = true
  FormatSpec = %.6g
  FormatSpecOverTolerance = %+.6g
  FormatSpecUnderTolerance = %+.6g
  Inverted = false
  LockPosition = false
  MeasureType = 1
  OverTolerance = 0
  References2D = -> [View002]
  Rotation = 0
  ScaleType = 0
  TheoreticalExact = false
  Type = 1
  UnderTolerance = 0
  X = -16.765
  Y = -22.8164
FEATURE [TechDraw::DrawViewDimension] Dimension028
  Arbitrary = false
  ArbitraryTolerances = false
  EqualTolerance = true
  FormatSpec = %.6g
  FormatSpecOverTolerance = %+.6g
  FormatSpecUnderTolerance = %+.6g
  Inverted = false
  LockPosition = false
  MeasureType = 1
  OverTolerance = 0
  References2D = -> [View002]
  Rotation = 0
  ScaleType = 0
  TheoreticalExact = false
  Type = 6
  UnderTolerance = 0
  X = 12.6302
  Y = 2.62915
FEATURE [TechDraw::DrawViewDimension] Dimension030
  Arbitrary = false
  ArbitraryTolerances = false
  EqualTolerance = true
  FormatSpec = %.6g
  FormatSpecOverTolerance = %+.6g
  FormatSpecUnderTolerance = %+.6g
  Inverted = false
  LockPosition = false
  MeasureType = 1
  OverTolerance = 0
  References2D = -> [ProjItem]
  Rotation = 0
  ScaleType = 0
  TheoreticalExact = false
  Type = 2
  UnderTolerance = 0
  X = -55.0499
  Y = 24.5331
FEATURE [TechDraw::DrawPage] Page001  label="Page2"
  KeepUpdated = true
  NextBalloonIndex = 1
  ProjectionType = 0
  Template = -> Template001
  Views = -> [ProjGroup,Dimension009,Dimension010,Dimension011,Dimension013,Dimension014,Dimension015,RichTextAnnotation,ProjGroup001,Dimension016,Dimension017,Dimension018,RichTextAnnotation001,ProjGroup002,ProjGroup003,ProjGroup004,Dimension021,View002,Annotation,Dimension022,Dimension023,Dimension024,RichTextAnnotation002,Dimension025,Dimension026,Dimension027,Dimension028,Dimension030]
FEATURE [PartDesign::CoordinateSystem] LCS_1  label="LCS_up"
  AttacherType = Attacher::AttachEngine3D
  Placement = pos=(0,0,300) rot=(0,0,1;0rad)
  expr: .Placement.Base.z = Variables.height
FEATURE [TechDraw::DrawViewAnnotation] Annotation001
  Font = osifont
  LineSpace = 80
  LockPosition = false
  MaxWidth = -1
  Rotation = 0
  ScaleType = 0
  Text = Plodi\u0161\u010dna naklada: |  - vi\u0161ina naklade = 300 mm |  - vi\u0161ina okvirja = 300 mm | Medi\u0161\u010dna naklada - optimizirana: |  - vi\u0161ina naklade = 200 mm |  - vi\u0161ina okvirja = 190 mm | Medi\u0161\u010dna naklada - standardna: |  - vi\u0161ina naklade = 175 mm |  - vi\u0161ina okvirja = 165 mm
  TextSize = 5
  TextStyle = 0
  X = 166.698
  Y = 85.5258
FEATURE [PartDesign::CoordinateSystem] LCS_0010
  AttacherType = Attacher::AttachEngine3D
  MapMode = 2
  Support = -> [X_Axis011]
FEATURE [PartDesign::CoordinateSystem] LCS_0011
  AttacherType = Attacher::AttachEngine3D
  MapMode = 2
  Support = -> [X_Axis012]
FEATURE [Sketcher::SketchObject] Sketch008  label="Sketch009"
  FullyConstrained = true
  MapMode = 5
  Placement = pos=(0,0,0) rot=(0.57735,0.57735,0.57735;2.0944rad)
  Support = -> [YZ_Plane012]
  expr: Constraints[22] = Variables.height - Variables.frame_cut
  sketch-geometry (8):
    g0: LineSegment StartX=-235 StartY=294 StartZ=0 EndX=235 EndY=294 EndZ=0
    g1: LineSegment StartX=235 StartY=294 StartZ=0 EndX=235 EndY=285 EndZ=0
    g2: LineSegment StartX=235 StartY=285 StartZ=0 EndX=207.5 EndY=285 EndZ=0
    g3: LineSegment StartX=207.5 StartY=285 StartZ=0 EndX=207.5 EndY=276 EndZ=0
    g4: LineSegment StartX=207.5 StartY=276 StartZ=0 EndX=-207.5 EndY=276 EndZ=0
    g5: LineSegment StartX=-207.5 StartY=276 StartZ=0 EndX=-207.5 EndY=285 EndZ=0
    g6: LineSegment StartX=-207.5 StartY=285 StartZ=0 EndX=-235 EndY=285 EndZ=0
    g7: LineSegment StartX=-235 StartY=285 StartZ=0 EndX=-235 EndY=294 EndZ=0
  constraints (23):
    c: Horizontal(g0)
    c: Coincident(g0,g1)
    c: Vertical(g1)
    c: Coincident(g1,g2)
    c: Horizontal(g2)
    c: Coincident(g2,g3)
    c: Vertical(g3)
    c: Coincident(g3,g4)
    c: Horizontal(g4)
    c: Coincident(g4,g5)
    c: Vertical(g5)
    c: Coincident(g5,g6)
    c: Coincident(g6,g7)
    c: Coincident(g7,g0)
    c: Horizontal(g6)
    c: Vertical(g7)
    c: Symmetric(g5,g2,g-2)
    c: Equal(g6,g2)
    c: DistanceX(g0,g0) = 470
    c: DistanceX(g5,g2) = 415
    c: DistanceY(g1,g1) = 9
    c: DistanceY(g3,g0) = 18
    c: DistanceY(g-1,g6) = 285
FEATURE [PartDesign::Pad] Pad005
  Direction = (1,1,1)
  Length = 25
  Length2 = 100
  Midplane = true
  Placement = pos=(0,0,0) rot=(0.57735,0.57735,0.57735;2.0944rad)
  Profile = -> Sketch008
  Type = 0
FEATURE [Sketcher::SketchObject] Sketch010  label="Sketch011"
  ExternalGeometry = -> [Pad005]
  FullyConstrained = true
  MapMode = 5
  Placement = pos=(-9.13e-14,-207.5,4.57e-14) rot=(-0.57735,-0.57735,0.57735;4.18879rad)
  Support = -> [Pad005]
  expr: Constraints[21] = Variables.frame_height
  sketch-geometry (8):
    g0: LineSegment StartX=-285 StartY=18 StartZ=0 EndX=-285 EndY=-18 EndZ=0
    g1: LineSegment StartX=-285 StartY=-18 StartZ=0 EndX=-185 EndY=-18 EndZ=0
    g2: LineSegment StartX=-185 StartY=-18 StartZ=0 EndX=-179.5 EndY=-12.5 EndZ=0
    g3: LineSegment StartX=-179.5 StartY=-12.5 StartZ=0 EndX=6 EndY=-12.5 EndZ=0
    g4: LineSegment StartX=6 StartY=-12.5 StartZ=0 EndX=6 EndY=12.5 EndZ=0
    g5: LineSegment StartX=6 StartY=12.5 StartZ=0 EndX=-179.5 EndY=12.5 EndZ=0
    g6: LineSegment StartX=-179.5 StartY=12.5 StartZ=0 EndX=-185 EndY=18 EndZ=0
    g7: LineSegment StartX=-185 StartY=18 StartZ=0 EndX=-285 EndY=18 EndZ=0
  constraints (22):
    c: Coincident(g0,g1)
    c: Horizontal(g1)
    c: Coincident(g1,g2)
    c: Coincident(g2,g3)
    c: Horizontal(g3)
    c: Coincident(g3,g4)
    c: Coincident(g4,g5)
    c: Horizontal(g5)
    c: Coincident(g5,g6)
    c: Coincident(g6,g7)
    c: Coincident(g7,g0)
    c: Horizontal(g7)
    c: Vertical(g5,g2)
    c: Vertical(g1,g6)
    c: Symmetric(g0,g0,g-1)
    c: Symmetric(g4,g3,g-1)
    c: Perpendicular(g6,g2)
    c: DistanceY(g4,g4) = 25
    c: DistanceY(g0,g0) = 36
    c: DistanceX(g7,g7) = 100
    c: PointOnObject(g-3,g0)
    c: DistanceX(g-3,g4) = 300
FEATURE [PartDesign::Pad] Pad006
  BaseFeature = -> Pad005
  Direction = (1,1,1)
  Length = 10
  Length2 = 100
  Placement = pos=(0,0,0) rot=(0.57735,0.57735,0.57735;2.0944rad)
  Profile = -> Sketch010
  Type = 0
FEATURE [Sketcher::SketchObject] Sketch011  label="Sketch012"
  ExternalGeometry = -> [Pad006]
  FullyConstrained = true
  MapMode = 5
  Placement = pos=(9.13e-14,207.5,-4.57e-14) rot=(0.57735,0.57735,0.57735;4.18879rad)
  Support = -> [Pad006]
  sketch-geometry (8):
    g0: LineSegment StartX=-6 StartY=12.5 StartZ=0 EndX=179.5 EndY=12.5 EndZ=0
    g1: LineSegment StartX=179.5 StartY=12.5 StartZ=0 EndX=185 EndY=18 EndZ=0
    g2: LineSegment StartX=185 StartY=18 StartZ=0 EndX=285 EndY=18 EndZ=0
    g3: LineSegment StartX=285 StartY=18 StartZ=0 EndX=285 EndY=-18 EndZ=0
    g4: LineSegment StartX=285 StartY=-18 StartZ=0 EndX=185 EndY=-18 EndZ=0
    g5: LineSegment StartX=185 StartY=-18 StartZ=0 EndX=179.5 EndY=-12.5 EndZ=0
    g6: LineSegment StartX=179.5 StartY=-12.5 StartZ=0 EndX=-6 EndY=-12.5 EndZ=0
    g7: LineSegment StartX=-6 StartY=-12.5 StartZ=0 EndX=-6 EndY=12.5 EndZ=0
  constraints (17):
    c: Coincident(g-6,g0)
    c: Coincident(g0,g-3)
    c: Coincident(g0,g1)
    c: Coincident(g1,g-3)
    c: Coincident(g1,g2)
    c: Horizontal(g2)
    c: Coincident(g2,g3)
    c: Coincident(g3,g-5)
    c: Vertical(g3)
    c: Coincident(g3,g4)
    c: Coincident(g4,g-4)
    c: Coincident(g4,g5)
    c: Coincident(g5,g-4)
    c: Coincident(g5,g6)
    c: Coincident(g6,g-6)
    c: Coincident(g6,g7)
    c: Coincident(g7,g0)
FEATURE [PartDesign::Pad] Pad007
  BaseFeature = -> Pad006
  Direction = (1,1,1)
  Length = 10
  Length2 = 100
  Placement = pos=(0,0,0) rot=(0.57735,0.57735,0.57735;2.0944rad)
  Profile = -> Sketch011
  Type = 0
FEATURE [Sketcher::SketchObject] Sketch012  label="Sketch013"
  ExternalGeometry = -> [Pad007]
  FullyConstrained = true
  MapMode = 5
  Placement = pos=(0,0,0) rot=(0.57735,0.57735,0.57735;2.0944rad)
  Support = -> [YZ_Plane012]
  sketch-geometry (4):
    g0: LineSegment StartX=-207.5 StartY=10 StartZ=0 EndX=207.5 EndY=10 EndZ=0
    g1: LineSegment StartX=207.5 StartY=10 StartZ=0 EndX=207.5 EndY=-6 EndZ=0
    g2: LineSegment StartX=207.5 StartY=-6 StartZ=0 EndX=-207.5 EndY=-6 EndZ=0
    g3: LineSegment StartX=-207.5 StartY=-6 StartZ=0 EndX=-207.5 EndY=10 EndZ=0
  constraints (10):
    c: Coincident(g0,g1)
    c: Coincident(g1,g2)
    c: Coincident(g2,g3)
    c: Coincident(g3,g0)
    c: Horizontal(g0)
    c: Vertical(g1)
    c: Vertical(g3)
    c: Coincident(g1,g-4)
    c: Coincident(g2,g-3)
    c: DistanceY(g1,g1) = 16
FEATURE [PartDesign::Pad] Pad008
  BaseFeature = -> Pad007
  Direction = (1,1,1)
  Length = 16
  Length2 = 100
  Midplane = true
  Placement = pos=(0,0,0) rot=(0.57735,0.57735,0.57735;2.0944rad)
  Profile = -> Sketch012
  Type = 0
FEATURE [PartDesign::Body] Body_5
  Group = -> [LCS_0011,Sketch008,Pad005,Sketch010,Pad006,Sketch011,Pad007,Sketch012,Pad008]
  Origin = -> Origin012
  Tip = -> Pad008
FEATURE [PartDesign::CoordinateSystem] LCS_L
  AttacherType = Attacher::AttachEngine3D
  Placement = pos=(-18.75,0,0) rot=(0,0,1;0rad)
  expr: .Placement.Base.x = -Variables.frame_spacing / 2
FEATURE [PartDesign::CoordinateSystem] LCS_R
  AttacherType = Attacher::AttachEngine3D
  Placement = pos=(18.75,0,0) rot=(0,0,1;0rad)
  expr: .Placement.Base.x = Variables.frame_spacing / 2
FEATURE [App::Part] frame
  Group = -> [LCS_0010,Body_5,LCS_L,LCS_R]
  Origin = -> Origin011
FEATURE [App::DocumentObjectGroup] Parts
  Group = -> [Wall_rear,wall_side,Slat,Slat2,Slat2004,frame]
FEATURE [App::Link] frame001  label="frame5"
  AssemblyType = Part::Link
  AttachedBy = #LCS_R
  AttachedTo = Parent Assembly#LCS_Origin
  LinkPlacement = pos=(-18.75,0,0) rot=(0,0,1;0rad)
  LinkedObject = -> frame
  Placement = pos=(-18.75,0,0) rot=(0,0,1;0rad)
  SolverId = Asm4EE
  expr: Placement = LCS_Origin.Placement * AttachmentOffset * LCS_R.Placement ^ -1
FEATURE [App::Link] frame4
  AssemblyType = Part::Link
  AttachedBy = #LCS_R
  AttachedTo = frame001#LCS_L
  LinkPlacement = pos=(-56.25,0,0) rot=(0,0,1;0rad)
  LinkedObject = -> frame
  Placement = pos=(-56.25,0,0) rot=(0,0,1;0rad)
  SolverId = Asm4EE
  expr: Placement = frame001.Placement * LCS_L.Placement * AttachmentOffset * LCS_R.Placement ^ -1
FEATURE [App::Link] frame3
  AssemblyType = Part::Link
  AttachedBy = #LCS_R
  AttachedTo = frame4#LCS_L
  LinkPlacement = pos=(-93.75,0,0) rot=(0,0,1;0rad)
  LinkedObject = -> frame
  Placement = pos=(-93.75,0,0) rot=(0,0,1;0rad)
  SolverId = Asm4EE
  expr: Placement = frame4.Placement * LCS_L.Placement * AttachmentOffset * LCS_R.Placement ^ -1
FEATURE [App::Link] frame2
  AssemblyType = Part::Link
  AttachedBy = #LCS_R
  AttachedTo = frame3#LCS_L
  LinkPlacement = pos=(-131.25,0,0) rot=(0,0,1;0rad)
  LinkedObject = -> frame
  Placement = pos=(-131.25,0,0) rot=(0,0,1;0rad)
  SolverId = Asm4EE
  expr: Placement = frame3.Placement * LCS_L.Placement * AttachmentOffset * LCS_R.Placement ^ -1
FEATURE [App::Link] fra  label="frame1"
  AssemblyType = Part::Link
  AttachedBy = #LCS_R
  AttachedTo = frame2#LCS_L
  LinkPlacement = pos=(-168.75,0,0) rot=(0,0,1;0rad)
  LinkedObject = -> frame
  Placement = pos=(-168.75,0,0) rot=(0,0,1;0rad)
  SolverId = Asm4EE
  expr: Placement = frame2.Placement * LCS_L.Placement * AttachmentOffset * LCS_R.Placement ^ -1
FEATURE [App::Link] frame_6
  AssemblyType = Part::Link
  AttachedBy = #LCS_L
  AttachedTo = frame001#LCS_R
  LinkPlacement = pos=(18.75,0,0) rot=(0,0,1;0rad)
  LinkedObject = -> frame
  Placement = pos=(18.75,0,0) rot=(0,0,1;0rad)
  SolverId = Asm4EE
  expr: Placement = frame001.Placement * LCS_R.Placement * AttachmentOffset * LCS_L.Placement ^ -1
FEATURE [App::Link] frame7
  AssemblyType = Part::Link
  AttachedBy = #LCS_L
  AttachedTo = frame_6#LCS_R
  LinkPlacement = pos=(56.25,0,0) rot=(0,0,1;0rad)
  LinkedObject = -> frame
  Placement = pos=(56.25,0,0) rot=(0,0,1;0rad)
  SolverId = Asm4EE
  expr: Placement = frame_6.Placement * LCS_R.Placement * AttachmentOffset * LCS_L.Placement ^ -1
FEATURE [App::Link] frame8
  AssemblyType = Part::Link
  AttachedBy = #LCS_L
  AttachedTo = frame7#LCS_R
  LinkPlacement = pos=(93.75,0,0) rot=(0,0,1;0rad)
  LinkedObject = -> frame
  Placement = pos=(93.75,0,0) rot=(0,0,1;0rad)
  SolverId = Asm4EE
  expr: Placement = frame7.Placement * LCS_R.Placement * AttachmentOffset * LCS_L.Placement ^ -1
FEATURE [App::Link] frame9
  AssemblyType = Part::Link
  AttachedBy = #LCS_L
  AttachedTo = frame8#LCS_R
  LinkPlacement = pos=(131.25,0,0) rot=(0,0,1;0rad)
  LinkedObject = -> frame
  Placement = pos=(131.25,0,0) rot=(0,0,1;0rad)
  SolverId = Asm4EE
  expr: Placement = frame8.Placement * LCS_R.Placement * AttachmentOffset * LCS_L.Placement ^ -1
FEATURE [App::Link] frame10
  AssemblyType = Part::Link
  AttachedBy = #LCS_L
  AttachedTo = frame9#LCS_R
  LinkPlacement = pos=(168.75,0,0) rot=(0,0,1;0rad)
  LinkedObject = -> frame
  Placement = pos=(168.75,0,0) rot=(0,0,1;0rad)
  SolverId = Asm4EE
  expr: Placement = frame9.Placement * LCS_R.Placement * AttachmentOffset * LCS_L.Placement ^ -1
FEATURE [App::Part] Assembly
  AssemblyType = Part::Link
  Group = -> [LCS_Origin,Constraints,Configurations,Wall_rear001,Wall_rear002,wall_side001,wall,Slat003,Slat2001,Slat2002,Slat2003,Handle1,Handle2,LCS_1,frame001,frame4,frame3,frame2,fra,frame_6,frame7,frame8,frame9,frame10]
  LabelDocUser = naklada
  LabelPartUser = Assembly
  Origin = -> Origin
  Type = Assembly
FEATURE [TechDraw::DrawViewPart] View001
  CoarseView = false
  Direction = (0,0,1)
  Focus = 100
  HardHidden = false
  IsoCount = 0
  IsoHidden = false
  IsoVisible = false
  LockPosition = false
  Perspective = false
  Rotation = 0
  Scale = 0.2
  ScaleType = 0
  SeamHidden = false
  SeamVisible = true
  SmoothHidden = false
  SmoothVisible = true
  Source = -> [Assembly]
  X = 75
  XDirection = (1,0,0)
  Y = 210
FEATURE [TechDraw::DrawViewSection] SectionView  label="Section A"
  BaseView = -> View001
  CoarseView = false
  CutSurfaceDisplay = 2
  Direction = (-1,0,0)
  FileGeomPattern = <path>
  FileHatchPattern = <path>
  Focus = 100
  FuseBeforeCut = false
  HardHidden = false
  HatchScale = 1
  IsoCount = 0
  IsoHidden = false
  IsoVisible = false
  LockPosition = false
  NameGeomPattern = Diamond
  Perspective = false
  Rotation = 0
  Scale = 0.2
  ScaleType = 0
  SeamHidden = false
  SeamVisible = true
  SectionDirection = 0
  SectionNormal = (-1,0,0)
  SectionOrigin = (0,225,148.5)
  SectionSymbol = A
  SmoothHidden = false
  SmoothVisible = true
  Source = -> [Assembly]
  X = 170
  XDirection = (0,0,1)
  Y = 210
FEATURE [TechDraw::DrawViewPart] View
  CoarseView = false
  Direction = (0.577,-0.577,0.577)
  Focus = 100
  HardHidden = false
  IsoCount = 0
  IsoHidden = false
  IsoVisible = false
  LockPosition = false
  Perspective = false
  Rotation = 0
  Scale = 0.1
  ScaleType = 0
  SeamHidden = false
  SeamVisible = true
  SmoothHidden = false
  SmoothVisible = true
  Source = -> [Assembly]
  X = 68.8094
  XDirection = (0.707,0.707,0)
  Y = 80.9578
FEATURE [TechDraw::DrawViewDimension] Dimension
  Arbitrary = false
  ArbitraryTolerances = false
  EqualTolerance = true
  FormatSpec = %.6g
  FormatSpecOverTolerance = %+.6g
  FormatSpecUnderTolerance = %+.6g
  Inverted = false
  LockPosition = false
  MeasureType = 1
  OverTolerance = 0
  References2D = -> [View001]
  Rotation = 0
  ScaleType = 0
  TheoreticalExact = false
  Type = 1
  UnderTolerance = 0
  X = 1.44839
  Y = 78.7851
FEATURE [TechDraw::DrawViewDimension] Dimension031
  Arbitrary = false
  ArbitraryTolerances = false
  EqualTolerance = true
  FormatSpec = %.6g
  FormatSpecOverTolerance = %+.6g
  FormatSpecUnderTolerance = %+.6g
  Inverted = false
  LockPosition = false
  MeasureType = 1
  OverTolerance = 0
  References2D = -> [View001]
  Rotation = 0
  ScaleType = 0
  TheoreticalExact = false
  Type = 2
  UnderTolerance = 0
  X = 52.5519
  Y = 2.38728
FEATURE [TechDraw::DrawViewDimension] Dimension032
  Arbitrary = false
  ArbitraryTolerances = false
  EqualTolerance = true
  FormatSpec = %.6g
  FormatSpecOverTolerance = %+.6g
  FormatSpecUnderTolerance = %+.6g
  Inverted = false
  LockPosition = false
  MeasureType = 1
  OverTolerance = 0
  References2D = -> [SectionView]
  Rotation = 0
  ScaleType = 0
  TheoreticalExact = false
  Type = 1
  UnderTolerance = 0
  X = 1.02479
  Y = -59.6162
FEATURE [TechDraw::DrawViewDimension] Dimension033
  Arbitrary = false
  ArbitraryTolerances = false
  EqualTolerance = true
  FormatSpec = %.6g
  FormatSpecOverTolerance = %+.6g
  FormatSpecUnderTolerance = %+.6g
  Inverted = false
  LockPosition = false
  MeasureType = 0
  OverTolerance = 0
  References2D = -> [View]
  References3D = -> [Assembly]
  Rotation = 0
  ScaleType = 0
  TheoreticalExact = false
  Type = 0
  UnderTolerance = 0
  X = 43.828
  Y = 30.2017
FEATURE [TechDraw::DrawPage] Page  label="Page1"
  KeepUpdated = true
  NextBalloonIndex = 1
  ProjectionType = 0
  Template = -> Template
  Views = -> [View,View001,SectionView,Annotation001,Dimension,Dimension031,Dimension032,Dimension033]
FEATURE [TechDraw::DrawSVGTemplate] Template002
  EditableTexts = AVTOR=Brane Borštnik; AVTOR_2=Risal: Janez Paternoster; DATUM=6.5.2022; MATERIAL=Les, smreka; MERILO=1:5; NAZIV=Okvir; NAZIV_2=Dadant-Blatt panj; STRAN=Stran 3/3; VIR=https://github.com/<owner>/Dadant-Blatt
  Height = 297
  Orientation = 0
  Width = 210
FEATURE [TechDraw::DrawViewPart] View003
  CoarseView = false
  Direction = (1,0,0)
  Focus = 100
  HardHidden = false
  IsoCount = 0
  IsoHidden = false
  IsoVisible = false
  LockPosition = false
  Perspective = false
  Rotation = 0
  Scale = 0.2
  ScaleType = 0
  SeamHidden = false
  SeamVisible = true
  SmoothHidden = false
  SmoothVisible = true
  Source = -> [frame]
  X = 90.8967
  XDirection = (0,1,0)
  Y = 150
FEATURE [TechDraw::DrawViewSection] SectionView001  label="Section A - A"
  BaseView = -> View003
  CoarseView = false
  CutSurfaceDisplay = 2
  Direction = (0,-1,0)
  FileGeomPattern = <path>
  FileHatchPattern = <path>
  Focus = 100
  FuseBeforeCut = false
  HardHidden = false
  HatchScale = 1
  IsoCount = 0
  IsoHidden = false
  IsoVisible = false
  LockPosition = false
  NameGeomPattern = Diamant
  Perspective = false
  Rotation = 0
  Scale = 0.2
  ScaleType = 0
  SeamHidden = false
  SeamVisible = true
  SectionDirection = 0
  SectionNormal = (0,-1,0)
  SectionOrigin = (0,0,144)
  SectionSymbol = A
  SmoothHidden = false
  SmoothVisible = true
  Source = -> [frame]
  X = 174.457
  XDirection = (1,0,0)
  Y = 150.441
FEATURE [TechDraw::DrawViewDimension] Dimension034
  Arbitrary = false
  ArbitraryTolerances = false
  EqualTolerance = true
  FormatSpec = %.6g
  FormatSpecOverTolerance = %+.6g
  FormatSpecUnderTolerance = %+.6g
  Inverted = false
  LockPosition = false
  MeasureType = 1
  OverTolerance = 0
  References2D = -> [View003]
  Rotation = 0
  Scale = 0.2
  ScaleType = 0
  TheoreticalExact = false
  Type = 1
  UnderTolerance = 0
  X = -2.20365
  Y = 60.6307
FEATURE [TechDraw::DrawViewDimension] Dimension035
  Arbitrary = false
  ArbitraryTolerances = false
  EqualTolerance = true
  FormatSpec = %.6g
  FormatSpecOverTolerance = %+.6g
  FormatSpecUnderTolerance = %+.6g
  Inverted = false
  LockPosition = false
  MeasureType = 1
  OverTolerance = 0
  References2D = -> [View003]
  Rotation = 0
  Scale = 0.2
  ScaleType = 0
  TheoreticalExact = false
  Type = 1
  UnderTolerance = 0
  X = -1.32219
  Y = -51.155
FEATURE [TechDraw::DrawViewDimension] Dimension036
  Arbitrary = false
  ArbitraryTolerances = false
  EqualTolerance = true
  FormatSpec = %.6g
  FormatSpecOverTolerance = %+.6g
  FormatSpecUnderTolerance = %+.6g
  Inverted = false
  LockPosition = false
  MeasureType = 1
  OverTolerance = 0
  References2D = -> [View003]
  Rotation = 0
  Scale = 0.2
  ScaleType = 0
  TheoreticalExact = false
  Type = 2
  UnderTolerance = 0
  X = -24.3116
  Y = -41.6219
FEATURE [TechDraw::DrawViewDimension] Dimension037
  Arbitrary = false
  ArbitraryTolerances = false
  EqualTolerance = true
  FormatSpec = %.6g
  FormatSpecOverTolerance = %+.6g
  FormatSpecUnderTolerance = %+.6g
  Inverted = false
  LockPosition = false
  MeasureType = 1
  OverTolerance = 0
  References2D = -> [View003]
  Rotation = 0
  Scale = 0.2
  ScaleType = 0
  TheoreticalExact = false
  Type = 1
  UnderTolerance = 0
  X = -51.535
  Y = -6.8617
FEATURE [TechDraw::DrawViewDimension] Dimension038
  Arbitrary = false
  ArbitraryTolerances = false
  EqualTolerance = true
  FormatSpec = %.6g
  FormatSpecOverTolerance = %+.6g
  FormatSpecUnderTolerance = %+.6g
  Inverted = false
  LockPosition = false
  MeasureType = 1
  OverTolerance = 0
  References2D = -> [View003]
  Rotation = 0
  Scale = 0.2
  ScaleType = 0
  TheoreticalExact = false
  Type = 2
  UnderTolerance = 0
  X = -55.5942
  Y = 42.3219
FEATURE [TechDraw::DrawViewDimension] Dimension039
  Arbitrary = false
  ArbitraryTolerances = false
  EqualTolerance = true
  FormatSpec = %.6g
  FormatSpecOverTolerance = %+.6g
  FormatSpecUnderTolerance = %+.6g
  Inverted = false
  LockPosition = false
  MeasureType = 1
  OverTolerance = 0
  References2D = -> [View003]
  Rotation = 0
  Scale = 0.2
  ScaleType = 0
  TheoreticalExact = false
  Type = 2
  UnderTolerance = 0
  X = -63.3161
  Y = 41.8626
FEATURE [TechDraw::DrawViewDimension] Dimension040
  Arbitrary = false
  ArbitraryTolerances = false
  EqualTolerance = true
  FormatSpec = %.6g
  FormatSpecOverTolerance = %+.6g
  FormatSpecUnderTolerance = %+.6g
  Inverted = false
  LockPosition = false
  MeasureType = 1
  OverTolerance = 0
  References2D = -> [View003]
  Rotation = 0
  Scale = 0.2
  ScaleType = 0
  TheoreticalExact = false
  Type = 2
  UnderTolerance = 0
  X = 51.7143
  Y = 4.18693
FEATURE [TechDraw::DrawViewDimension] Dimension041
  Arbitrary = false
  ArbitraryTolerances = false
  EqualTolerance = true
  FormatSpec = %.6g
  FormatSpecOverTolerance = %+.6g
  FormatSpecUnderTolerance = %+.6g
  Inverted = false
  LockPosition = false
  MeasureType = 1
  OverTolerance = 0
  References2D = -> [SectionView001]
  Rotation = 0
  Scale = 0.2
  ScaleType = 0
  TheoreticalExact = false
  Type = 1
  UnderTolerance = 0
  X = -0.440729
  Y = 57.766
FEATURE [TechDraw::DrawViewDimension] Dimension042
  Arbitrary = false
  ArbitraryTolerances = false
  EqualTolerance = true
  FormatSpec = %.6g
  FormatSpecOverTolerance = %+.6g
  FormatSpecUnderTolerance = %+.6g
  Inverted = false
  LockPosition = false
  MeasureType = 1
  OverTolerance = 0
  References2D = -> [SectionView001]
  Rotation = 0
  Scale = 0.2
  ScaleType = 0
  TheoreticalExact = false
  Type = 1
  UnderTolerance = 0
  X = 13.6626
  Y = 23.8459
FEATURE [TechDraw::DrawViewDimension] Dimension043
  Arbitrary = false
  ArbitraryTolerances = false
  EqualTolerance = true
  FormatSpec = %.6g
  FormatSpecOverTolerance = %+.6g
  FormatSpecUnderTolerance = %+.6g
  Inverted = false
  LockPosition = false
  MeasureType = 1
  OverTolerance = 0
  References2D = -> [SectionView001]
  Rotation = 0
  Scale = 0.2
  ScaleType = 0
  TheoreticalExact = false
  Type = 1
  UnderTolerance = 0
  X = 7.4924
  Y = -37.8182
FEATURE [TechDraw::DrawRichAnno] RichTextAnnotation003
  AnnoParent = -> SectionView001
  AnnoText = <!DOCTYPE HTML PUBLIC "-//W3C//DTD HTML 4.0//EN" "http://www.w3.org/TR/REC-html40/strict.dtd">\n<html><head><meta name="qrichtext" content="1" /><style type="text/css">\np, li { white-space: pre-wrap; }\n</style></head><body style=" font-family:'Ubuntu'; font-size:11pt; font-weight:400; font-style:normal;">\n<p style=" margin-top:0px; margin-bottom:0px; margin-left:0px; margin-right:0px; -qt-block-indent:0; text-indent:0px;"><span style=" font-size:10pt;">Prerez A-A</span></p></body></html>
  LockPosition = false
  MaxWidth = -1
  Rotation = 0
  Scale = 0.2
  ScaleType = 0
  ShowFrame = false
  X = 1.44838
  Y = -51.4177
FEATURE [TechDraw::DrawViewDimension] Dimension044
  Arbitrary = false
  ArbitraryTolerances = false
  EqualTolerance = true
  FormatSpec = %.6g
  FormatSpecOverTolerance = %+.6g
  FormatSpecUnderTolerance = %+.6g
  Inverted = false
  LockPosition = false
  MeasureType = 1
  OverTolerance = 0
  References2D = -> [SectionView001]
  Rotation = 0
  Scale = 0.2
  ScaleType = 0
  TheoreticalExact = false
  Type = 2
  UnderTolerance = 0
  X = -18.9181
  Y = 20.753
FEATURE [TechDraw::DrawPage] Page002  label="Page3"
  KeepUpdated = true
  NextBalloonIndex = 1
  ProjectionType = 0
  Scale = 0.2
  Template = -> Template002
  Views = -> [View003,SectionView001,Dimension034,Dimension035,Dimension036,Dimension037,Dimension038,Dimension039,Dimension040,Dimension041,Dimension042,Dimension043,RichTextAnnotation003,Dimension044]
note: 4 file-system paths scrubbed to <path> (originals preserved in the JSON sidecar)
